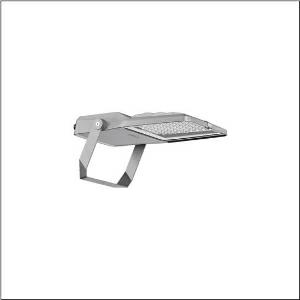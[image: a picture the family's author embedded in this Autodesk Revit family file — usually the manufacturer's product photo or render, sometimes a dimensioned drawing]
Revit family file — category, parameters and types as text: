
# Revit family: floodlight_fl_21_mini___pl43_5xa7772b3a1a_26e5
name_source: partatom
category: Lighting Fixtures
units: mm (PartAtom-declared; Revit-internal decimal feet)

## family parameters
Cut with Voids When Loaded = No
Host = Face
Light Source = No
Part Type = Normal
Room Calculation Point = No
Round Connector Dimension = Use Diameter
Shared = No

## types (1)
- --- (1 x LED, 5510 lm, 45.5 W, 3000K)
    Apparent Load = 46 VA
    CIE Flux Codes = 27 78 99 100 100
    Color Rendering = 80
    Color Temperature = 3000K
    Default Elevation = 1800 mm
    Description = Floodlight FL 21 mini, floodlight, primary light control with lens, of PMMA, primary optical cover: protective disc, of toughened safety glass, transparent, light distribution: PL43, light emission: direct distribution, installation type: surface-mounted, LED, High Power LED, rated luminous flux: 5.510lm, luminous efficacy: 121lm/W, light colour: 830, colour temperature: 3000K, control gear: ECG iQ, control: Street-Remote, Auto-Match, Temp-Guard, Night-Set, Smart-Wire, Desk-Remote (wireless, voltage-free reading and setting of iQ features in the workshop via application-optimized NFC function/RFID function), optimised constant luminous flux control (CLO 2.0), with terminal, 6-pole, mains connection: 220..240V, AC, 50/60Hz, start of lifetime: 46W, end of lifetime: 48W, reduction: 21W, luminaire housing, of diecast aluminium, powder-coated, Siteco® metallic grey (DB 702S), corrosivity category C5 according to DIN EN ISO 12944, mounting bracket, of steel, galvanised, powder-coated, Siteco® metallic grey (DB 702S), protection rating (complete): IP66, insulation class (complete): insulation class II (safety insulation), certification: CE, ENEC, VDE, protection symbol: D, impact resistance: IK08, permissible operating ambient temperature: -40..+40°C, permissible operating ambient temperature for outdoor applications: -40..+50°C, standard: DIN EN 12944, packaging unit: 1 piece

Light Distribution: PL43
    Height = 70 mm
    Lamp = 1 x LED
    Lamp Light Flux = 5510 lm
    Lamp Power = 45.5 W
    Lamp count = 1
    Length = 485 mm
    Luminous efficacy = 121 lm/W
    Manufacturer = Siteco
    ModVariant = No
    Model = 5XA7772B3A1A
    Number of Poles = 1
    OnlyDefault = Yes
    Power Factor = 1
    Product Name = Floodlight FL 21 mini | PL43
    Product group = floodlight | pylon top
    ProductGroupID = 6101
    Protection Class = Protection class II
    Protection Degree = IP 66
    RLX_Detail_Level = 1
    RlxData = <blob elided: 95977 chars, md5=594fe4a9>
    Socket = socket
    Standby Power = 0 W
    System Light Flux = 5510 lm
    System Power = 46 W
    Type Comments = factory setting: luminous flux: 100 % | dim-lin: 254 | 463 mA
    Type Image = l_1006845.jpg
    URL = http://relux.com
    VarID = @adj_073941
    Voltage = 0 V
    Weight = 0.00 kg
    Width = 337 mm

## geometry (parser evidence)
native form markers: Blend x4, Sweep x10
no freeform markers — native parametric forms only
